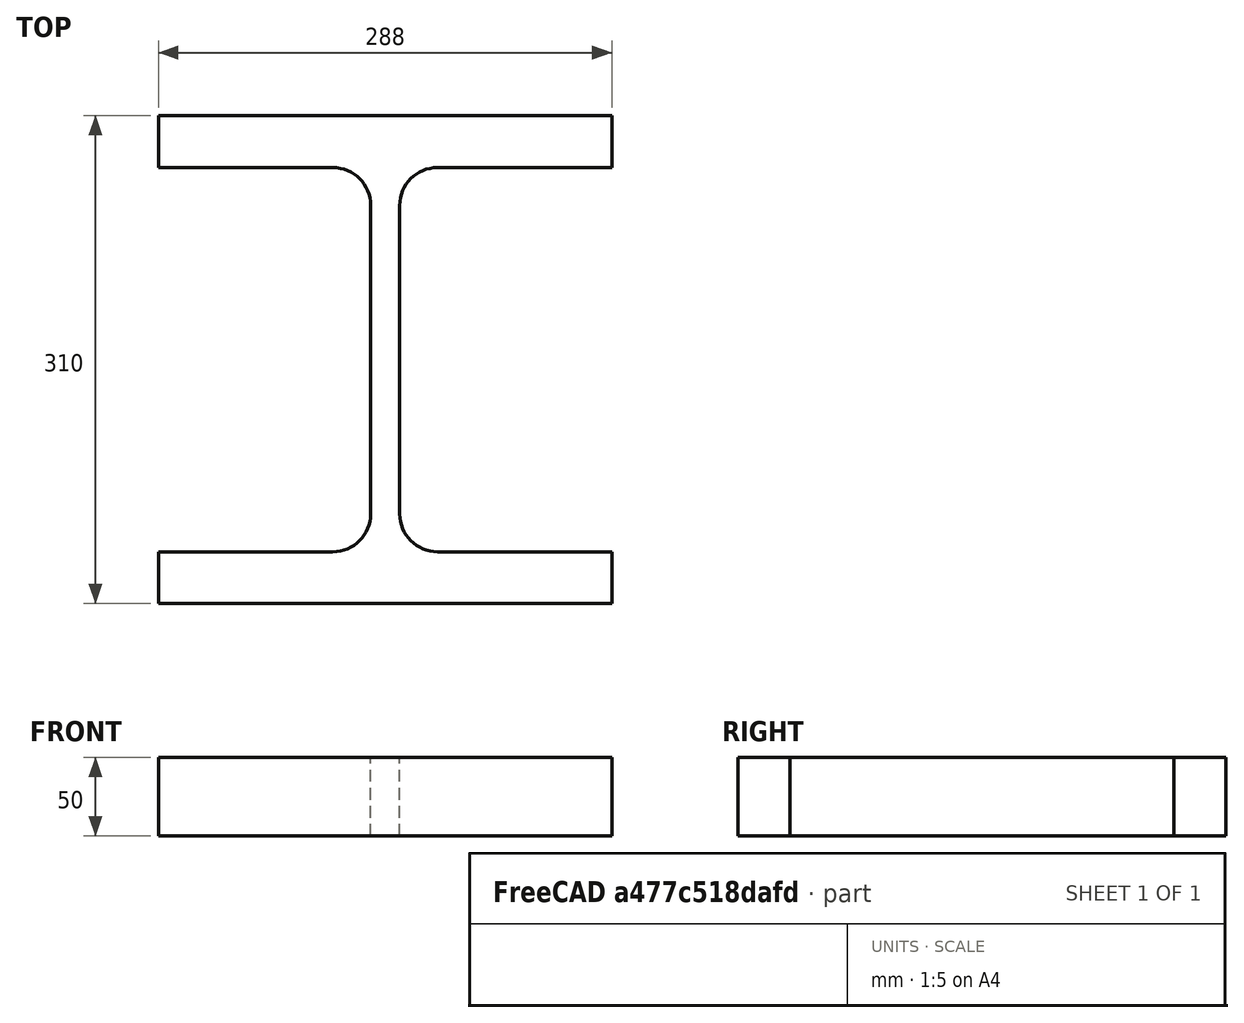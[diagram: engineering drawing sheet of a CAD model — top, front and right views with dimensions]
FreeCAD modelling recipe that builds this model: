
FCSTD DOCUMENT  (FreeCAD 0.15R4671 (Git))
Label: HE-M-Profile 280 DIN1025-4 S235JR
License: All rights reserved
LicenseURL: http://en.wikipedia.org/wiki/All_rights_reserved
objects: Sketcher::SketchObject×1, Part::Extrusion×1
note: 2 computed .brp shape members not serialized (recipe doc carries the construction recipe); baked Part::Feature solids carry a one-line shape summary decoded from their .brp

FEATURE [Sketcher::SketchObject] Sketch
  sketch-geometry (16):
    g0: LineSegment StartX=9.25 StartY=-98 StartZ=0 EndX=9.25 EndY=98 EndZ=0
    g1: LineSegment StartX=33.25 StartY=122 StartZ=0 EndX=144 EndY=122 EndZ=0
    g2: LineSegment StartX=144 StartY=122 StartZ=0 EndX=144 EndY=155 EndZ=0
    g3: LineSegment StartX=144 StartY=155 StartZ=0 EndX=-144 EndY=155 EndZ=0
    g4: LineSegment StartX=-144 StartY=155 StartZ=0 EndX=-144 EndY=122 EndZ=0
    g5: LineSegment StartX=-144 StartY=122 StartZ=0 EndX=-33.25 EndY=122 EndZ=0
    g6: LineSegment StartX=-9.25 StartY=98 StartZ=0 EndX=-9.25 EndY=-98 EndZ=0
    g7: LineSegment StartX=-33.25 StartY=-122 StartZ=0 EndX=-144 EndY=-122 EndZ=0
    g8: LineSegment StartX=-144 StartY=-122 StartZ=0 EndX=-144 EndY=-155 EndZ=0
    g9: LineSegment StartX=-144 StartY=-155 StartZ=0 EndX=144 EndY=-155 EndZ=0
    g10: LineSegment StartX=144 StartY=-155 StartZ=0 EndX=144 EndY=-122 EndZ=0
    g11: LineSegment StartX=144 StartY=-122 StartZ=0 EndX=33.25 EndY=-122 EndZ=0
    g12: ArcOfCircle CenterX=33.25 CenterY=98 CenterZ=0 NormalX=0 NormalY=0 NormalZ=1 Radius=24 StartAngle=1.5708 EndAngle=3.14159
    g13: ArcOfCircle CenterX=33.25 CenterY=-98 CenterZ=0 NormalX=0 NormalY=0 NormalZ=1 Radius=24 StartAngle=3.14159 EndAngle=4.71239
    g14: ArcOfCircle CenterX=-33.25 CenterY=98 CenterZ=0 NormalX=0 NormalY=0 NormalZ=1 Radius=24 StartAngle=0 EndAngle=1.5708
    g15: ArcOfCircle CenterX=-33.25 CenterY=-98 CenterZ=0 NormalX=0 NormalY=0 NormalZ=1 Radius=24 StartAngle=4.71239 EndAngle=6.28319
  constraints (42):
    c: Vertical(g0)
    c: Coincident(g2,g1)
    c: Vertical(g2)
    c: Coincident(g3,g2)
    c: Coincident(g4,g3)
    c: Vertical(g4)
    c: Coincident(g5,g4)
    c: Horizontal(g5)
    c: Vertical(g6)
    c: Horizontal(g7)
    c: Coincident(g8,g7)
    c: Vertical(g8)
    c: Coincident(g9,g8)
    c: Horizontal(g9)
    c: Coincident(g10,g9)
    c: Vertical(g10)
    c: Coincident(g11,g10)
    c: Horizontal(g11)
    c: Tangent(g1,g12) = 1.5708
    c: Tangent(g0,g12) = 1.5708
    c: Tangent(g0,g13) = 1.5708
    c: Tangent(g11,g13) = 1.5708
    c: Tangent(g5,g14) = 1.5708
    c: Tangent(g6,g14) = 1.5708
    c: Tangent(g6,g15) = 1.5708
    c: Tangent(g7,g15) = 1.5708
    c: Equal(g3,g9)
    c: Equal(g2,g4)
    c: Equal(g4,g8)
    c: Equal(g8,g10)
    c: Equal(g12,g14)
    c: Equal(g14,g15)
    c: Equal(g15,g13)
    c: Symmetric(g2,g3,g-2)
    c: Symmetric(g9,g8,g-2)
    c: Symmetric(g0,g6,g-2)
    c: Symmetric(g2,g9,g-1)
    c: DistanceY(g2,g9) = -310
    c: DistanceX(g3) = -288
    c: DistanceX(g0,g6) = -18.5
    c: DistanceY(g2) = 33
    c: Radius(g12) = 24
FEATURE [Part::Extrusion] Extrude  label="HE-M-Profile 280 DIN1025-4 S235JR"
  Base = -> Sketch
  Dir = (0,0,50)
  Solid = true
